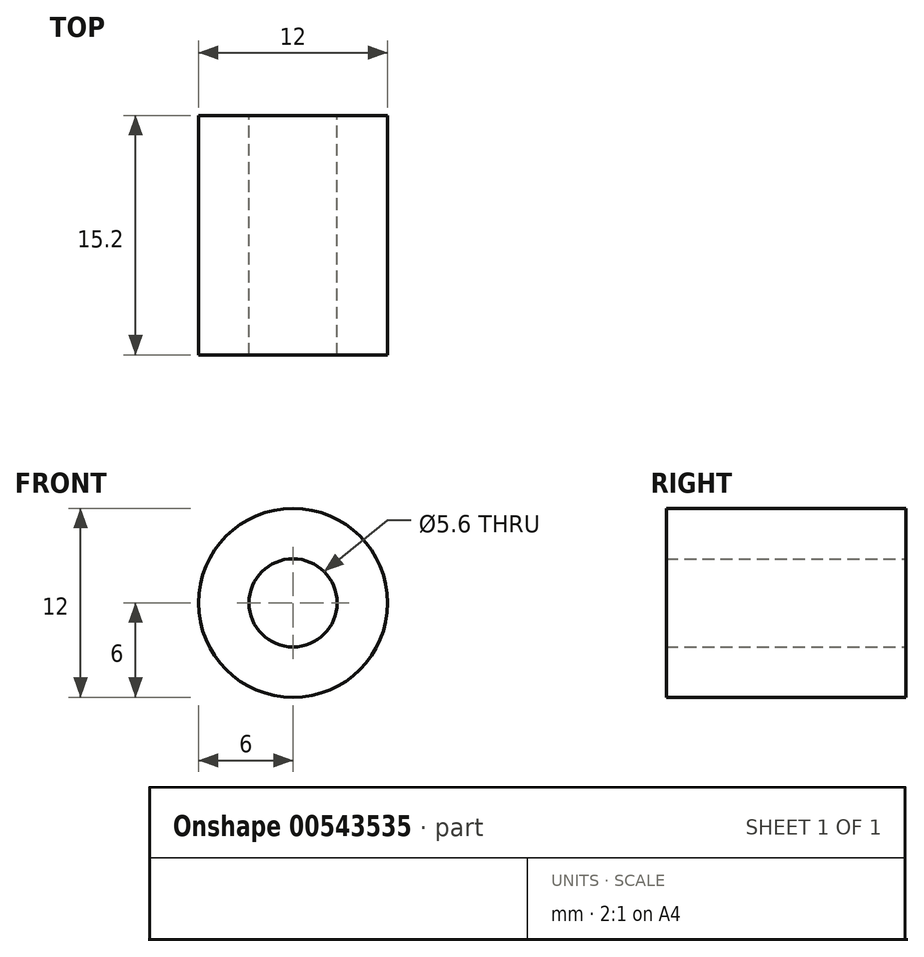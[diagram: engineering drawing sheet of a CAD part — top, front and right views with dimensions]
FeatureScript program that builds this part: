
annotation { "Feature Type Name" : "Feature", "Feature Type Description" : "" }
export const myFeature = defineFeature(function(context is Context, id is Id, definition is map)
    precondition{}
    {
        {
            var Q0;
            Q0=qCreatedBy(makeId("Front.planeOp"),FACE);
            var sketch = newSketch(context, id + "F0", { "sketchPlane" : qUnion([Q0])});
            skCircle(sketch, "E0", {"center": v(0, 0) * mm, "radius": 2.8 * mm});
            skCircle(sketch, "E1", {"center": v(0, 0) * mm, "radius": 6 * mm});
            skSolve(sketch);
        }
        {
            var Q0;
            Q0=makeQuery(id+"F0.imprint","IMPRINT",FACE,{"disambiguationData":[TD([[makeQuery(id+"F0.imprint","IMPRINT",EDGE,{"derivedFrom":sQuery(id+"F0.wireOp",EDGE,"E0")}),-1.0]])]});
            extrude(context, id + "F1", {"entities" : qUnion([Q0]), "depth" : 15.2 * mm, "offsetDistance" : 25 * mm});
        }
    });
